# Revit family: Legrand_Gestion_eclairage_Detecteur_Presence_Plafond_autonome_R3
name_source: partatom
category: Dispositifs d'éclairage
units: mm (PartAtom-declared; Revit-internal decimal feet)

## family parameters
Conserver l'orientation des annotations = Non
Cote de connecteur circulaire = Utiliser le diamètre
Couper avec des vides une fois chargée = Non
Hôte = Face
Partagée = Non
Point de calcul de pièce = Non
Type d'élément = Normal

## types (16) — shared parameters
COULOIR_PIR = INTERDETECTEUR_COULOIR_PIR
Conditions Générale d'Utilisation = https://export.legrand.com
Couleur = Blanc
DOUBLE_TECHNO = INTERDETECTEUR_DOUBLE-TECHNO_RACC_VIS
Elévation par défaut = 1219 mm
FAUX_PLAFOND_PIR = DETECTEUR_FAUX_PLAFOND_PIR
Fabricant = LEGRAND
IP55 = ECODETECTEUR_IP55_ECO_2_GRANDE_HAUTEUR
IR_360 = INTERDETECTEUR_IR_360
IR_360_45_M_2 = INTERDETECTEUR_IR_360_45_M_2
Luminosité de déclenchement ajustable = Oui
MW_FAUX_PLAFOND = DETECTEUR_MW_FAUX_PLAFOND
Mode de pose = Encastré
PIR_COMPACT = DETECTEUR_PIR_COMPACT
PIR_MID_RANGE = DETECTEUR_PIR_MID_RANGE
PIR_MINI = DETECTEUR_PIR_MINI
Régulation de la lumière = Oui
Sensibilité ajustable = Oui
URL = www.legrand.fr

## per-type parameters (varying)
- MID RANGE-IR - 360° - 1-10V: Adapté pour transmission sans fil=Non; Angle de détection horizontal=360-360 °; Commandable à distance=Oui; Commande HVAC=Non; Commande auxiliaire possible=Oui; Courrant de démarrage MAX=80 A; DETECTEUR=DETECTEUR_PIR_MID_RANGE; Diamètre=76 mm  [stored 0.249344 ft]; Diamètre de détection au sol=15000 mm  [stored 49.2126 ft]; Durée de marche max.=99; Durée de marche min.=0.5; Désignation produit=DETECTEUR PIR MOYENNE PORTEE VARIATION 1-10V & COMMUTATION; Fréquence=50 Hz; Gestion d'alarme=Non; Hauteur=0 mm  [stored 0 ft]; Hauteur Optimale=2800 mm  [stored 9.18635 ft]; IK=05; IP=40; Largeur=76 mm  [stored 0.249344 ft]; Largeur de portée max.=7500 mm  [stored 24.6063 ft]; Longueur de portée max.=7500 mm  [stored 24.6063 ft]; Luminosité de déclenchement=0-2000 lx; Modèle de Produit=detecteur de presence; PETITE_ZONE=Non; Profondeur=77 mm  [stored 0.252625 ft]; Puissance de coupure max.=2300 W; Référence / Modèle=LG-048969; Temperature d'utilisation MIN-MAX=-10/+30 °C; Tension=230 AC; Type de capteur=infrarouge; Télécommandable=Oui
- MID RANGE-IR - 360° - DALI: Adapté pour transmission sans fil=Non; Angle de détection horizontal=360-360 °; Commandable à distance=Oui; Commande HVAC=Non; Commande auxiliaire possible=Oui; Courrant de démarrage MAX=80 A; DETECTEUR=DETECTEUR_PIR_MID_RANGE; Diamètre=76 mm  [stored 0.249344 ft]; Diamètre de détection au sol=15000 mm  [stored 49.2126 ft]; Durée de marche max.=99; Durée de marche min.=0.5; Désignation produit=DETECTEUR PIR MOYENNE PORTEE VARIATION DALI & COMMUTATION; Fréquence=50 Hz; Gestion d'alarme=Non; Hauteur=0 mm  [stored 0 ft]; Hauteur Optimale=2800 mm  [stored 9.18635 ft]; IK=05; IP=40; Largeur=76 mm  [stored 0.249344 ft]; Largeur de portée max.=7500 mm  [stored 24.6063 ft]; Longueur de portée max.=7500 mm  [stored 24.6063 ft]; Luminosité de déclenchement=0-2000 lx; Modèle de Produit=detecteur de presence; PETITE_ZONE=Non; Profondeur=77 mm  [stored 0.252625 ft]; Puissance de coupure max.=2300 W; Référence / Modèle=LG-048968; Temperature d'utilisation MIN-MAX=-10/+30 °C; Tension=230 AC; Type de capteur=infrarouge; Télécommandable=Oui
- MID RANGE-IR - 360° - 2 Canaux: Adapté pour transmission sans fil=Non; Angle de détection horizontal=360-360 °; Commandable à distance=Oui; Commande HVAC=Non; Commande auxiliaire possible=Oui; Courrant de démarrage MAX=80 A; DETECTEUR=DETECTEUR_PIR_MID_RANGE; Diamètre=76 mm  [stored 0.249344 ft]; Diamètre de détection au sol=15000 mm  [stored 49.2126 ft]; Durée de marche max.=99; Durée de marche min.=0.5; Désignation produit=DETECTEUR PIR MOYENNE PORTEE COMMUTATION 2 CANAUX; Fréquence=50 Hz; Gestion d'alarme=Non; Hauteur=0 mm  [stored 0 ft]; Hauteur Optimale=2800 mm  [stored 9.18635 ft]; IK=05; IP=40; Largeur=76 mm  [stored 0.249344 ft]; Largeur de portée max.=7500 mm  [stored 24.6063 ft]; Longueur de portée max.=7500 mm  [stored 24.6063 ft]; Luminosité de déclenchement=0-2000 lx; Modèle de Produit=detecteur de presence; PETITE_ZONE=Non; Profondeur=70 mm; Puissance de coupure max.=1300 W; Référence / Modèle=LG-048970; Temperature d'utilisation MIN-MAX=-10/+30 °C; Tension=230 AC; Type de capteur=infrarouge; Télécommandable=Oui
- MINI-IR - 360° - 1-10V: Adapté pour transmission sans fil=Non; Angle de détection horizontal=360-360 °; Commandable à distance=Oui; Commande HVAC=Non; Commande auxiliaire possible=Oui; Courrant de démarrage MAX=80 A; DETECTEUR=DETECTEUR_PIR_MINI; Diamètre=28 mm  [stored 0.0918635 ft]; Diamètre de détection au sol=7000 mm  [stored 22.9659 ft]; Durée de marche max.=99; Durée de marche min.=0.5; Désignation produit=DETECTEUR PIR MINIATURE VARIATION 1-10V & COMMUTATION; Fréquence=50 Hz; Gestion d'alarme=Non; Hauteur=0 mm  [stored 0 ft]; Hauteur Optimale=2800 mm  [stored 9.18635 ft]; IK=05; IP=40; Largeur=76 mm  [stored 0.249344 ft]; Largeur de portée max.=3500 mm  [stored 11.4829 ft]; Longueur de portée max.=3500 mm  [stored 11.4829 ft]; Luminosité de déclenchement=0-2000 lx; Modèle de Produit=detecteur de presence; PETITE_ZONE=Oui; Profondeur=30 mm  [stored 0.0984252 ft]; Puissance de coupure max.=1300 W; Référence / Modèle=LG-048966; Temperature d'utilisation MIN-MAX=-10/+30 °C; Tension=230 AC; Type de capteur=infrarouge; Télécommandable=Oui
- MINI-IR - 360° - DALI: Adapté pour transmission sans fil=Non; Angle de détection horizontal=360-360 °; Commandable à distance=Oui; Commande HVAC=Non; Commande auxiliaire possible=Oui; Courrant de démarrage MAX=80 A; DETECTEUR=DETECTEUR_PIR_MINI; Diamètre=0 mm  [stored 0 ft]; Diamètre de détection au sol=7000 mm  [stored 22.9659 ft]; Durée de marche max.=0.1; Durée de marche min.=1; Désignation produit=DETECTEUR PIR MINI FAUX PLAFOND VARIATION DALI; Fréquence=50 Hz; Gestion d'alarme=Non; Hauteur=33 mm  [stored 0.108268 ft]; Hauteur Optimale=2800 mm  [stored 9.18635 ft]; IK=05; IP=40; Largeur=28 mm  [stored 0.0918635 ft]; Largeur de portée max.=7000 mm  [stored 22.9659 ft]; Longueur de portée max.=7000 mm  [stored 22.9659 ft]; Luminosité de déclenchement=0-2000 lx; Modèle de Produit=autre; PETITE_ZONE=Non; Profondeur=30 mm  [stored 0.0984252 ft]; Puissance de coupure max.=2400 W; Référence / Modèle=LG-048953; Temperature d'utilisation MIN-MAX=-10/+35 °C; Tension=230 AC; Type de capteur=infrarouge; Télécommandable=Oui
- MINI-IR - 360° - ON-OFF: Adapté pour transmission sans fil=Non; Angle de détection horizontal=360-360 °; Commandable à distance=Oui; Commande HVAC=Non; Commande auxiliaire possible=Oui; Courrant de démarrage MAX=80 A; DETECTEUR=DETECTEUR_PIR_MINI; Diamètre=0 mm  [stored 0 ft]; Diamètre de détection au sol=7000 mm  [stored 22.9659 ft]; Durée de marche max.=0.1; Durée de marche min.=1; Désignation produit=DETECTEUR PIR MINI FAUX PLAFOND ON-OFF; Fréquence=50 Hz; Gestion d'alarme=Non; Hauteur=33 mm  [stored 0.108268 ft]; Hauteur Optimale=2800 mm  [stored 9.18635 ft]; IK=05; IP=40; Largeur=28 mm  [stored 0.0918635 ft]; Largeur de portée max.=7000 mm  [stored 22.9659 ft]; Longueur de portée max.=7000 mm  [stored 22.9659 ft]; Luminosité de déclenchement=0-2000 lx; Modèle de Produit=autre; PETITE_ZONE=Non; Profondeur=30 mm  [stored 0.0984252 ft]; Puissance de coupure max.=2400 W; Référence / Modèle=LG-048954; Temperature d'utilisation MIN-MAX=-10/+35 °C; Tension=230 AC; Type de capteur=infrarouge; Télécommandable=Oui
- COMPACT-IR - 360° - 12-48V: Adapté pour transmission sans fil=Non; Angle de détection horizontal=360-360 °; Commandable à distance=Oui; Commande HVAC=Non; Commande auxiliaire possible=Oui; Courrant de démarrage MAX=80 A; DETECTEUR=DETECTEUR_PIR_COMPACT; Diamètre=0 mm  [stored 0 ft]; Diamètre de détection au sol=7000 mm  [stored 22.9659 ft]; Durée de marche max.=0.1; Durée de marche min.=1; Désignation produit=DETECTEUR PIR FAUX PLAFOND BAS TENSION; Fréquence=50 Hz; Gestion d'alarme=Non; Hauteur=65 mm  [stored 0.213255 ft]; Hauteur Optimale=2800 mm  [stored 9.18635 ft]; IK=05; IP=40; Largeur=76 mm  [stored 0.249344 ft]; Largeur de portée max.=7000 mm  [stored 22.9659 ft]; Longueur de portée max.=7000 mm  [stored 22.9659 ft]; Luminosité de déclenchement=0-2000 lx; Modèle de Produit=autre; PETITE_ZONE=Non; Profondeur=70 mm; Puissance de coupure max.=2400 W; Référence / Modèle=LG-048952; Temperature d'utilisation MIN-MAX=-10/+35 °C; Tension=24 AC/DC; Type de capteur=infrarouge; Télécommandable=Oui
- COMPACT-IR - 360° - DALI: Adapté pour transmission sans fil=Non; Angle de détection horizontal=360-360 °; Commandable à distance=Oui; Commande HVAC=Non; Commande auxiliaire possible=Oui; Courrant de démarrage MAX=80 A; DETECTEUR=DETECTEUR_PIR_COMPACT; Diamètre=76 mm  [stored 0.249344 ft]; Diamètre de détection au sol=7000 mm  [stored 22.9659 ft]; Durée de marche max.=99; Durée de marche min.=0.5; Désignation produit=DETECTEUR PIR COMPACT VARIATION DALI & COMMUTATION; Fréquence=50 Hz; Gestion d'alarme=Non; Hauteur=0 mm  [stored 0 ft]; Hauteur Optimale=2800 mm  [stored 9.18635 ft]; IK=05; IP=40; Largeur=76 mm  [stored 0.249344 ft]; Largeur de portée max.=3500 mm  [stored 11.4829 ft]; Longueur de portée max.=3500 mm  [stored 11.4829 ft]; Luminosité de déclenchement=0-2000 lx; Modèle de Produit=detecteur de presence; PETITE_ZONE=Oui; Profondeur=70 mm; Puissance de coupure max.=2300 W; Référence / Modèle=LG-048964; Temperature d'utilisation MIN-MAX=-10/+30 °C; Tension=230 AC; Type de capteur=infrarouge; Télécommandable=Oui
- COMPACT-IR - 360° - 1-10V: Adapté pour transmission sans fil=Non; Angle de détection horizontal=360-360 °; Commandable à distance=Oui; Commande HVAC=Non; Commande auxiliaire possible=Oui; Courrant de démarrage MAX=80 A; DETECTEUR=DETECTEUR_PIR_COMPACT; Diamètre=20 mm  [stored 0.0656168 ft]; Diamètre de détection au sol=7000 mm  [stored 22.9659 ft]; Durée de marche max.=99; Durée de marche min.=0.5; Désignation produit=DETECTEUR PIR COMPACT VARIATION 1-10V & COMMUTATION; Fréquence=50 Hz; Gestion d'alarme=Non; Hauteur=0 mm  [stored 0 ft]; Hauteur Optimale=2800 mm  [stored 9.18635 ft]; IK=05; IP=40; Largeur=76 mm  [stored 0.249344 ft]; Largeur de portée max.=3500 mm  [stored 11.4829 ft]; Longueur de portée max.=3500 mm  [stored 11.4829 ft]; Luminosité de déclenchement=0-2000 lx; Modèle de Produit=detecteur de presence; PETITE_ZONE=Oui; Profondeur=70 mm; Puissance de coupure max.=2300 W; Référence / Modèle=LG-048965; Temperature d'utilisation MIN-MAX=-10/+30 °C; Tension=230 AC; Type de capteur=infrarouge; Télécommandable=Oui
- MW-DALI-Tete Orientable: Adapté pour transmission sans fil=Non; Angle de détection horizontal=180-360 °; Commandable à distance=Oui; Commande HVAC=Non; Commande auxiliaire possible=Oui; Courrant de démarrage MAX=80 A; DETECTEUR=DETECTEUR_MW_FAUX_PLAFOND; Diamètre=0 mm  [stored 0 ft]; Diamètre de détection au sol=22000 mm  [stored 72.1785 ft]; Durée de marche max.=0.1; Durée de marche min.=1; Désignation produit=DETECTEUR MW FAUX PLAFOND VARIATION DALI TETE ORIENTABLE; Fréquence=50 Hz; Gestion d'alarme=Non; Hauteur=96 mm  [stored 0.314961 ft]; Hauteur Optimale=2600 mm  [stored 8.53018 ft]; IK=05; IP=40; Largeur=85 mm  [stored 0.278871 ft]; Largeur de portée max.=6000 mm  [stored 19.685 ft]; Longueur de portée max.=30000 mm  [stored 98.4252 ft]; Luminosité de déclenchement=0-2000 lx; Modèle de Produit=autre; PETITE_ZONE=Non; Profondeur=99 mm  [stored 0.324803 ft]; Puissance de coupure max.=2400 W; Référence / Modèle=LG-048957; Temperature d'utilisation MIN-MAX=-10/+35 °C; Tension=230 AC; Type de capteur=haute frequence; Télécommandable=Oui
- IR Grande Hauteur-Faible Temperature: Adapté pour transmission sans fil=Non; Angle de détection horizontal=360-360 °; Commandable à distance=Oui; Commande HVAC=Non; Commande auxiliaire possible=Oui; Courrant de démarrage MAX=80 A; DETECTEUR=DETECTEUR_FAUX_PLAFOND_PIR; Diamètre=0 mm  [stored 0 ft]; Diamètre de détection au sol=40000 mm  [stored 131.234 ft]; Durée de marche max.=0.1; Durée de marche min.=1; Désignation produit=DETECTEUR FAUX PLAFOND PIR GRAND HAUTEURS ET BASSES TEMPERATURES; Fréquence=50 Hz; Gestion d'alarme=Non; Hauteur=112 mm  [stored 0.367454 ft]; Hauteur Optimale=15000 mm  [stored 49.2126 ft]; IK=05; IP=40; Largeur=88 mm  [stored 0.288714 ft]; Largeur de portée max.=40000 mm  [stored 131.234 ft]; Longueur de portée max.=40000 mm  [stored 131.234 ft]; Luminosité de déclenchement=0-2000 lx; Modèle de Produit=autre; PETITE_ZONE=Non; Profondeur=112 mm  [stored 0.367454 ft]; Puissance de coupure max.=2400 W; Référence / Modèle=LG-048959; Temperature d'utilisation MIN-MAX=-30/+35 °C; Tension=230 AC; Type de capteur=infrarouge; Télécommandable=Oui
- Ecodétecteur IP55 ECO2 Grande Hauteur: Adapté pour transmission sans fil=Oui; Angle de détection horizontal=360-360 °; Commandable à distance=Oui; Commande HVAC=Non; Commande auxiliaire possible=Non; Courrant de démarrage MAX=8.5 A; DETECTEUR=ECODETECTEUR_IP55_ECO_2_GRANDE_HAUTEUR; Diamètre=122 mm  [stored 0.400262 ft]; Diamètre de détection au sol=25000 mm  [stored 82.021 ft]; Durée de marche max.=60; Durée de marche min.=5; Désignation produit=Ecodétecteur autonome ECO 2 1 circuit - IR- saillie plafond - IP 55 - Ø25m; Fréquence=50-60 Hz; Gestion d'alarme=Non; Hauteur=0 mm  [stored 0 ft]; Hauteur Optimale=10000 mm  [stored 32.8084 ft]; IK=04; IP=55; Largeur=0 mm  [stored 0 ft]; Largeur de portée max.=25000 mm  [stored 82.021 ft]; Longueur de portée max.=25000 mm  [stored 82.021 ft]; Luminosité de déclenchement=5-1275 lx; Modèle de Produit=detecteur de presence; PETITE_ZONE=Non; Profondeur=86 mm  [stored 0.282152 ft]; Puissance de coupure max.=2000 W; Référence / Modèle=LG-048932; Temperature d'utilisation MIN-MAX=-25/+45 °C; Tension=230 AC; Type de capteur=infrarouge; Télécommandable=Non
- Couloir PIR: Adapté pour transmission sans fil=Non; Angle de détection horizontal=0-360 °; Commandable à distance=Non; Commande HVAC=Non; Commande auxiliaire possible=Oui; Courrant de démarrage MAX=8.5 A; DETECTEUR=INTERDETECTEUR_COULOIR_PIR; Diamètre=122 mm  [stored 0.400262 ft]; Diamètre de détection au sol=24000 mm  [stored 78.7402 ft]; Durée de marche max.=59; Durée de marche min.=5; Désignation produit=Détect autonome ECO 2 Prog Mosaic - 1 circuit - faux plafond - spécial couloir; Fréquence=50-60 Hz; Gestion d'alarme=Oui; Hauteur=0 mm  [stored 0 ft]; Hauteur Optimale=2500 mm  [stored 8.2021 ft]; IK=04; IP=20; Largeur=0 mm  [stored 0 ft]; Largeur de portée max.=12000 mm  [stored 39.3701 ft]; Longueur de portée max.=3000 mm  [stored 9.84252 ft]; Luminosité de déclenchement=5-1275 lx; Modèle de Produit=Détecteur de Mouvement; PETITE_ZONE=Non; Profondeur=93 mm  [stored 0.305118 ft]; Puissance de coupure max.=2000 W; Référence / Modèle=LG-048817; Temperature d'utilisation MIN-MAX=-5/+45 °C; Tension=230 AC; Type de capteur=infrarouge; Télécommandable=Oui
- Double technologie - Racc Vis - 360° - 90 m²: Adapté pour transmission sans fil=Non; Angle de détection horizontal=0-360 °; Commandable à distance=Oui; Commande HVAC=Non; Commande auxiliaire possible=Oui; Courrant de démarrage MAX=8.5 A; DETECTEUR=INTERDETECTEUR_DOUBLE-TECHNO_RACC_VIS; Diamètre=122 mm  [stored 0.400262 ft]; Diamètre de détection au sol=8000 mm  [stored 26.2467 ft]; Durée de marche max.=59; Durée de marche min.=5; Désignation produit=Détect autonome ECO 2 Prog Mosaic-1 circ éclairage-faux plafond-auto-IR/US-90m²; Fréquence=50-60 Hz; Gestion d'alarme=Oui; Hauteur=0 mm  [stored 0 ft]; Hauteur Optimale=2500 mm  [stored 8.2021 ft]; IK=04; IP=20; Largeur=0 mm  [stored 0 ft]; Largeur de portée max.=4000 mm  [stored 13.1234 ft]; Longueur de portée max.=6000 mm  [stored 19.685 ft]; Luminosité de déclenchement=5-1275 lx; Modèle de Produit=detecteur de presence; PETITE_ZONE=Non; Profondeur=82 mm  [stored 0.269029 ft]; Puissance de coupure max.=2000 W; Référence / Modèle=LG-048806; Temperature d'utilisation MIN-MAX=-5/+45 °C; Tension=230 AC; Type de capteur=infrarouge et ultrason; Télécommandable=Non
- IR - 360°: Adapté pour transmission sans fil=Non; Angle de détection horizontal=0-360 °; Commandable à distance=Oui; Commande HVAC=Oui; Commande auxiliaire possible=Oui; Courrant de démarrage MAX=8.5 A; DETECTEUR=INTERDETECTEUR_IR_360; Diamètre=105 mm  [stored 0.344488 ft]; Diamètre de détection au sol=8000 mm  [stored 26.2467 ft]; Durée de marche max.=59; Durée de marche min.=5; Désignation produit=Inter détecteur mouv Prog. Mosaic-ECO2- 1 circ-plafd- IR- 3 fils+N - portée Ø8 m; Fréquence=50-60 Hz; Gestion d'alarme=Oui; Hauteur=0 mm  [stored 0 ft]; Hauteur Optimale=2500 mm  [stored 8.2021 ft]; IK=04; IP=20; Largeur=0 mm  [stored 0 ft]; Largeur de portée max.=4000 mm  [stored 13.1234 ft]; Longueur de portée max.=6000 mm  [stored 19.685 ft]; Luminosité de déclenchement=5-1275 lx; Modèle de Produit=Détecteur de Mouvement; PETITE_ZONE=Non; Profondeur=73 mm  [stored 0.239501 ft]; Puissance de coupure max.=2000 W; Référence / Modèle=LG-048804; Temperature d'utilisation MIN-MAX=-5/+45 °C; Tension=230 AC; Type de capteur=infrarouge; Télécommandable=Non
- IR - 360° - 45m²: Adapté pour transmission sans fil=Non; Angle de détection horizontal=0-360 °; Commandable à distance=Oui; Commande HVAC=Non; Commande auxiliaire possible=Oui; Courrant de démarrage MAX=8.5 A; DETECTEUR=INTERDETECTEUR_IR_360_45_M_2; Diamètre=102 mm; Diamètre de détection au sol=8000 mm  [stored 26.2467 ft]; Durée de marche max.=59; Durée de marche min.=5; Désignation produit=Détect autonome ECO 2 Prog Mosaic-1 circuit éclairage-faux plafond-auto-IR-45m²; Fréquence=50-60 Hz; Gestion d'alarme=Oui; Hauteur=0 mm  [stored 0 ft]; Hauteur Optimale=2500 mm  [stored 8.2021 ft]; IK=04; IP=20; Largeur=0 mm  [stored 0 ft]; Largeur de portée max.=4000 mm  [stored 13.1234 ft]; Longueur de portée max.=6000 mm  [stored 19.685 ft]; Luminosité de déclenchement=5-1275 lx; Modèle de Produit=Détecteur de Mouvement; PETITE_ZONE=Non; Profondeur=82 mm  [stored 0.269029 ft]; Puissance de coupure max.=2000 W; Référence / Modèle=LG-048807; Temperature d'utilisation MIN-MAX=-5/+45 °C; Tension=230 AC; Type de capteur=infrarouge; Télécommandable=Non

note: [stored X ft] marks values corroborated as IEEE doubles in the binary element streams (Revit-internal decimal feet)
